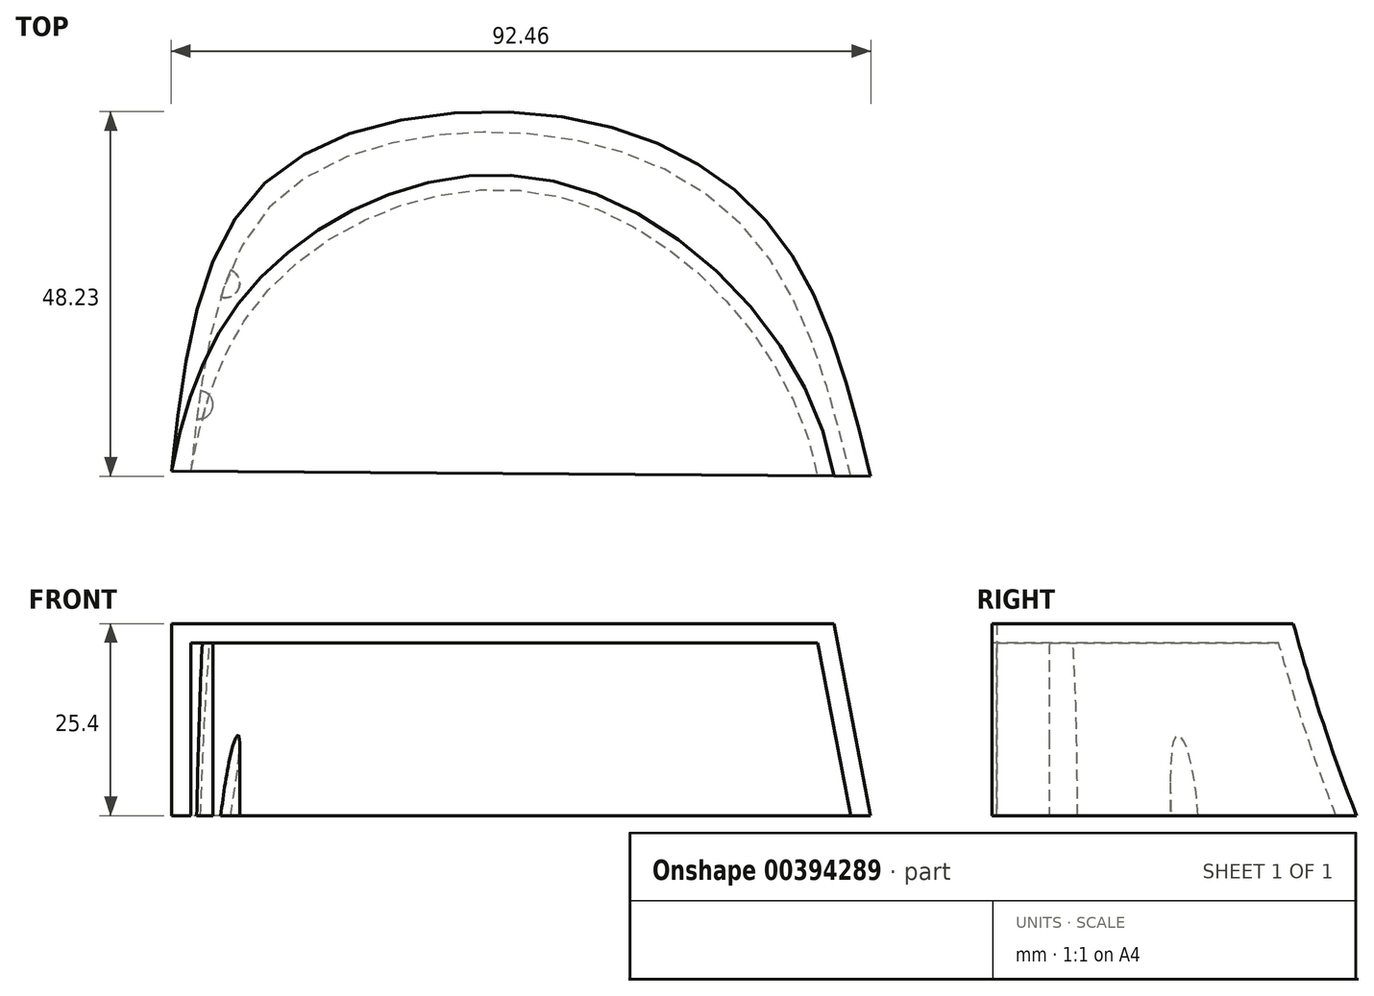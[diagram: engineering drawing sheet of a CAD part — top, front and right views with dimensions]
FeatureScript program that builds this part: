
annotation { "Feature Type Name" : "Feature", "Feature Type Description" : "" }
export const myFeature = defineFeature(function(context is Context, id is Id, definition is map)
    precondition{}
    {
        {
            var Q0;
            Q0=qCreatedBy(makeId("Top.planeOp"),FACE);
            var sketch = newSketch(context, id + "F0", { "sketchPlane" : qUnion([Q0])});
            skFitSpline(sketch, "E0", {"points": [v(-52.1, -31.09) * mm, v(-39.65, 7.13) * mm, v(0, 15.7) * mm, v(28.18, 0) * mm, v(40.35, -31.75) * mm], "startDerivative": vector(18.91, 170.15) * mm, "endDerivative": vector(35.56, -144.57) * mm});
            skLineSegment(sketch, "E1", {"start": v(-52.1, -31.09) * mm, "end": v(40.35, -31.75) * mm});
            skSolve(sketch);
        }
        {
            var Q0;
            Q0=qCreatedBy(makeId("Top.planeOp"),FACE);
            cPlane(context, id + "F1", {"entities" : qUnion([Q0]), "cplaneType" : CPlaneType.OFFSET, "offset" : 25.4 * mm, "width" : 152.4 * mm, "height" : 152.4 * mm});
        }
        {
            var Q0;
            Q0=qCreatedBy(id+"F1.planeOp",FACE);
            var sketch = newSketch(context, id + "F2", { "sketchPlane" : qUnion([Q0])});
            skFitSpline(sketch, "E2", {"points": [v(-52.1, -31.09) * mm, v(-37.53, -2.83) * mm, v(0, 6.93) * mm, v(35.46, -31.71) * mm], "startDerivative": vector(22, 121.55) * mm, "endDerivative": vector(21.7, -136.66) * mm});
            skLineSegment(sketch, "E3", {"start": v(-52.1, -31.09) * mm, "end": v(35.46, -31.71) * mm});
            skSolve(sketch);
        }
        {
            var Q0;
            Q0=makeQuery(id+"F2.imprint","IMPRINT",FACE,{"disambiguationData":[TD([[makeQuery(id+"F2.imprint","IMPRINT",EDGE,{"derivedFrom":sQuery(id+"F2.wireOp",EDGE,"E2")}),-1.0]])]});
            var Q1;
            Q1=makeQuery(id+"F0.imprint","IMPRINT",FACE,{"disambiguationData":[TD([[makeQuery(id+"F0.imprint","IMPRINT",EDGE,{"derivedFrom":sQuery(id+"F0.wireOp",EDGE,"E0")}),-1.0]])]});
            loft(context, id + "F3", {"sheetProfilesArray" : [{ "sheetProfileEntities" : qUnion([Q0]) }, { "sheetProfileEntities" : qUnion([Q1]) }]});
        }
        {
            var Q0;
            {var subQ0=sQuery(id+"F2.wireOp",EDGE,"E3");var subQ1=sQuery(id+"F2.wireOp",EDGE,"E2");var subQ2=sQuery(id+"F0.wireOp",EDGE,"E1");var subQ3=sQuery(id+"F0.wireOp",EDGE,"E0");Q0=makeQuery(id+"F3.opLoft","SWEPT_FACE",FACE,{"disambiguationData":[OSD([subQ3,subQ2,subQ1,subQ0]),TDD([makeQuery(id+"F0.imprint","INTERSECT",VERTEX,{"disambiguationData":[OD(0.0)],"derivedFrom":[subQ3,subQ2]}),makeQuery(id+"F0.imprint","INTERSECT",VERTEX,{"disambiguationData":[OD(1.0)],"derivedFrom":[subQ3,subQ2]}),makeQuery(id+"F0.imprint","IMPRINT",EDGE,{"derivedFrom":subQ2}),makeQuery(id+"F2.imprint","INTERSECT",VERTEX,{"disambiguationData":[OD(0.0)],"derivedFrom":[subQ1,subQ0]}),makeQuery(id+"F2.imprint","INTERSECT",VERTEX,{"disambiguationData":[OD(1.0)],"derivedFrom":[subQ1,subQ0]}),makeQuery(id+"F2.imprint","IMPRINT",EDGE,{"derivedFrom":subQ0})])]});}
            var Q1;
            Q1=makeQuery(id+"F3.opLoft","CAP_FACE",FACE,{"disambiguationData":[OSD([makeQuery(id+"F0.imprint","IMPRINT",FACE,{"disambiguationData":[TD([[makeQuery(id+"F0.imprint","IMPRINT",EDGE,{"derivedFrom":sQuery(id+"F0.wireOp",EDGE,"E0")}),-1.0]])]})])],"isStart":true});
            shell(context, id + "F4", {"entities" : qUnion([Q0, Q1]), "thickness" : 2.54 * mm});
        }
        {
            var Q0;
            Q0=makeQuery(id+"F3.opLoft","CAP_FACE",FACE,{"disambiguationData":[OSD([makeQuery(id+"F0.imprint","IMPRINT",FACE,{"disambiguationData":[TD([[makeQuery(id+"F0.imprint","IMPRINT",EDGE,{"derivedFrom":sQuery(id+"F0.wireOp",EDGE,"E0")}),-1.0]])]})])],"isStart":true});
            var sketch = newSketch(context, id + "F5", { "sketchPlane" : qUnion([Q0])});
            skCircle(sketch, "E4", {"center": v(-48.5, 22.3) * mm, "radius": 1.9 * mm});
            skCircle(sketch, "E5", {"center": v(-44.97, 6.24) * mm, "radius": 1.9 * mm});
            skSolve(sketch);
        }
        {
            var Q0;
            {var subQ0=sQuery(id+"F5.wireOp",EDGE,"E4");var subQ1=sQuery(id+"F0.wireOp",EDGE,"E0");var subQ2=sQuery(id+"F0.wireOp",EDGE,"E1");var subQ3=makeQuery(id+"F4.opShell","OFFSET_EDGE",EDGE,{"disambiguationData":[OSD([subQ1,subQ2]),TDD([makeQuery(id+"F3.opLoft","MID_CAP_EDGE",EDGE,{"disambiguationData":[OSD([subQ1,subQ2]),TDD([makeQuery(id+"F0.imprint","INTERSECT",VERTEX,{"disambiguationData":[OD(0.0)],"derivedFrom":[subQ1,subQ2]}),makeQuery(id+"F0.imprint","INTERSECT",VERTEX,{"disambiguationData":[OD(1.0)],"derivedFrom":[subQ1,subQ2]}),makeQuery(id+"F0.imprint","IMPRINT",EDGE,{"derivedFrom":subQ1})])],"capPos":1.0})])]});var subQ4=makeQuery(id+"F5.imprint","INTERSECT",VERTEX,{"disambiguationData":[OD(0.0)],"derivedFrom":[subQ3,subQ0]});Q0=makeQuery(id+"F5.imprint","IMPRINT",FACE,{"disambiguationData":[TD([[makeQuery(id+"F5.imprint","IMPRINT",EDGE,{"disambiguationData":[TD([[subQ4,1.0]])],"derivedFrom":subQ0}),1.0]])]});}
            var Q1;
            {var subQ0=sQuery(id+"F5.wireOp",EDGE,"E5");var subQ1=sQuery(id+"F0.wireOp",EDGE,"E0");var subQ2=sQuery(id+"F0.wireOp",EDGE,"E1");var subQ3=makeQuery(id+"F4.opShell","OFFSET_EDGE",EDGE,{"disambiguationData":[OSD([subQ1,subQ2]),TDD([makeQuery(id+"F3.opLoft","MID_CAP_EDGE",EDGE,{"disambiguationData":[OSD([subQ1,subQ2]),TDD([makeQuery(id+"F0.imprint","INTERSECT",VERTEX,{"disambiguationData":[OD(0.0)],"derivedFrom":[subQ1,subQ2]}),makeQuery(id+"F0.imprint","INTERSECT",VERTEX,{"disambiguationData":[OD(1.0)],"derivedFrom":[subQ1,subQ2]}),makeQuery(id+"F0.imprint","IMPRINT",EDGE,{"derivedFrom":subQ1})])],"capPos":1.0})])]});var subQ4=makeQuery(id+"F5.imprint","INTERSECT",VERTEX,{"disambiguationData":[OD(0.0)],"derivedFrom":[subQ3,subQ0]});Q1=makeQuery(id+"F5.imprint","IMPRINT",FACE,{"disambiguationData":[TD([[makeQuery(id+"F5.imprint","IMPRINT",EDGE,{"disambiguationData":[TD([[subQ4,-1.0]])],"derivedFrom":subQ0}),1.0]])]});}
            var Q2;
            Q2 = qConstructionFilter(qBodyType(qCreatedBy(id + "F5" ,EDGE), BodyType.WIRE), ConstructionObject.NO);
            var Q3;
            Q3=makeQuery(id+"F4.opShell","OFFSET_FACE",FACE,{"disambiguationData":[OSD([sQuery(id+"F0.wireOp",EDGE,"E0"),sQuery(id+"F0.wireOp",EDGE,"E1"),sQuery(id+"F2.wireOp",EDGE,"E2"),sQuery(id+"F2.wireOp",EDGE,"E3")])]});
            extrude(context, id + "F6", {"entities" : qUnion([Q0, Q1]), "surfaceEntities" : qUnion([Q2]), "endBound" : BoundingType.UP_TO_NEXT, "oppositeDirection" : true, "endBoundEntityFace" : qUnion([Q3]), "depth" : 25.4 * mm});
        }
    });
